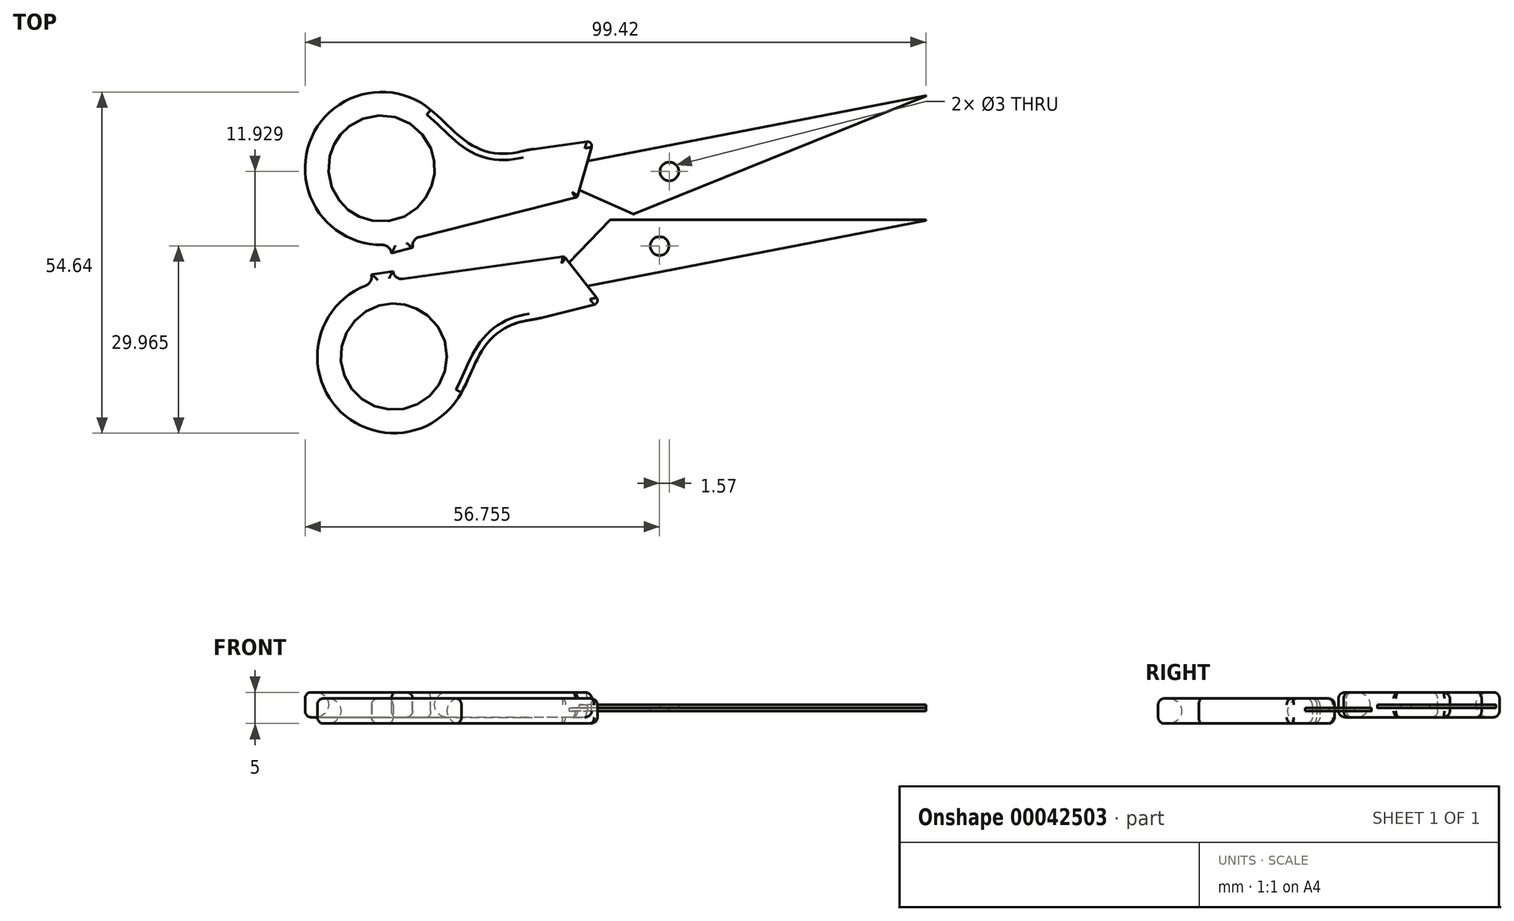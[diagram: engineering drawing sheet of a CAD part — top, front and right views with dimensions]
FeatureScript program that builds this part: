
annotation { "Feature Type Name" : "Feature", "Feature Type Description" : "" }
export const myFeature = defineFeature(function(context is Context, id is Id, definition is map)
    precondition{}
    {
        {
            var Q0;
            Q0=qCreatedBy(makeId("Top.planeOp"),FACE);
            var sketch = newSketch(context, id + "F0", { "sketchPlane" : qUnion([Q0])});
            skLineSegment(sketch, "E0", {"start": v(0.08, 0) * mm, "end": v(50.48, 0) * mm});
            skLineSegment(sketch, "E1", {"start": v(50.5, -0.1) * mm, "end": v(-3.64, -10.62) * mm});
            skLineSegment(sketch, "E2", {"start": v(-0.06, -0.06) * mm, "end": v(-6.6, -6.83) * mm});
            skLineSegment(sketch, "E3", {"start": v(-6.6, -6.83) * mm, "end": v(-3.64, -10.62) * mm});
            skPoint(sketch, "E4.visualSharp", {"position": v(51, 0) * mm});
            skArc(sketch, "E4.filletArc", {"start": v(50.5, -0.1) * mm, "mid": v(50.53, -0.05) * mm, "end": v(50.48, 0) * mm});
            skPoint(sketch, "E5.visualSharp", {"position": v(0, 0) * mm});
            skArc(sketch, "E5.filletArc", {"start": v(0.08, 0) * mm, "mid": v(0, -0.02) * mm, "end": v(-0.06, -0.06) * mm});
            skLineSegment(sketch, "E6", {"start": v(-6.6, -6.83) * mm, "end": v(-7.16, -6.12) * mm});
            skLineSegment(sketch, "E7", {"start": v(-3.64, -10.62) * mm, "end": v(-2.2, -12.47) * mm});
            skLineSegment(sketch, "E8", {"start": v(-3.64, -10.62) * mm, "end": v(-34.65, -21.9) * mm, "construction": true});
            skCircle(sketch, "E9", {"center": v(-34.65, -21.9) * mm, "radius": 8.5 * mm});
            skCircle(sketch, "E10", {"center": v(-34.65, -21.9) * mm, "radius": 12.25 * mm, "construction": true});
            skLineSegment(sketch, "E11", {"start": v(-7.62, -5.93) * mm, "end": v(-33.2, -9.47) * mm});
            skLineSegment(sketch, "E12", {"start": v(-2.58, -13.58) * mm, "end": v(-10.9, -15.66) * mm});
            skFitSpline(sketch, "E13", {"points": [v(-23.83, -27.66) * mm, v(-12.03, -15.94) * mm], "startDerivative": vector(7.63, 13.41) * mm, "endDerivative": vector(25.84, 2.61) * mm});
            skLineSegment(sketch, "E14", {"start": v(-34.65, -21.9) * mm, "end": v(-18.73, -30.37) * mm, "construction": true});
            skLineSegment(sketch, "E15", {"start": v(-34.77, -8.27) * mm, "end": v(-34.77, -8.27) * mm});
            skLineSegment(sketch, "E16", {"start": v(-34.77, -8.27) * mm, "end": v(-38.24, -8.75) * mm});
            skLineSegment(sketch, "E17", {"start": v(-38.24, -8.75) * mm, "end": v(-38.21, -8.91) * mm});
            skArc(sketch, "E18", {"start": v(-39.15, -10.51) * mm, "mid": v(-43.79, -30.07) * mm, "end": v(-23.83, -27.66) * mm});
            skPoint(sketch, "E19.visualSharp", {"position": v(-1.53, -13.32) * mm});
            skArc(sketch, "E19.filletArc", {"start": v(-2.58, -13.58) * mm, "mid": v(-2.08, -13.13) * mm, "end": v(-2.2, -12.47) * mm});
            skPoint(sketch, "E20.visualSharp", {"position": v(-7.34, -5.89) * mm});
            skArc(sketch, "E20.filletArc", {"start": v(-7.16, -6.12) * mm, "mid": v(-7.37, -5.96) * mm, "end": v(-7.62, -5.93) * mm});
            skPoint(sketch, "E21.visualSharp", {"position": v(-34.58, -9.66) * mm});
            skArc(sketch, "E21.filletArc", {"start": v(-34.77, -8.27) * mm, "mid": v(-34.23, -9.2) * mm, "end": v(-33.2, -9.47) * mm});
            skPoint(sketch, "E22.visualSharp", {"position": v(-38.05, -10.14) * mm});
            skArc(sketch, "E22.filletArc", {"start": v(-39.15, -10.51) * mm, "mid": v(-38.4, -9.88) * mm, "end": v(-38.21, -8.91) * mm});
            skPoint(sketch, "E23", {"position": v(13.7, -7.25) * mm});
            skArc(sketch, "E24.filletArc", {"start": v(-12.8, -16.04) * mm, "mid": v(-11.85, -15.87) * mm, "end": v(-10.9, -15.66) * mm});
            skSolve(sketch);
        }
        {
            var Q0;
            Q0=makeQuery(id+"F0.imprint","IMPRINT",FACE,{"disambiguationData":[TD([[makeQuery(id+"F0.imprint","IMPRINT",EDGE,{"derivedFrom":sQuery(id+"F0.wireOp",EDGE,"E0")}),-1.0]])]});
            extrude(context, id + "F1", {"entities" : qUnion([Q0]), "depth" : 0.5 * mm});
        }
        {
            var Q0;
            Q0=makeQuery(id+"F0.imprint","IMPRINT",FACE,{"disambiguationData":[TD([[makeQuery(id+"F0.imprint","IMPRINT",EDGE,{"derivedFrom":sQuery(id+"F0.wireOp",EDGE,"E3")}),-1.0]])]});
            extrude(context, id + "F2", {"entities" : qUnion([Q0]), "operationType" : NewBodyOperationType.ADD, "endBound" : BoundingType.SYMMETRIC, "depth" : 4 * mm});
        }
        {
            var Q0;
            Q0=makeQuery(id+"F2.opExtrude","CAP_EDGE",EDGE,{"disambiguationData":[OSD([sQuery(id+"F0.wireOp",EDGE,"E3"),sQuery(id+"F0.wireOp",EDGE,"E6"),sQuery(id+"F0.wireOp",EDGE,"E7")])],"isStart":false});
            var Q1;
            Q1=makeQuery(id+"F2.opExtrude","CAP_EDGE",EDGE,{"disambiguationData":[OSD([sQuery(id+"F0.wireOp",EDGE,"E11")])],"isStart":false});
            var Q2;
            Q2=makeQuery(id+"F2.opExtrude","CAP_EDGE",EDGE,{"disambiguationData":[OSD([sQuery(id+"F0.wireOp",EDGE,"E18")])],"isStart":false});
            var Q3;
            Q3=makeQuery(id+"F2.opExtrude","CAP_EDGE",EDGE,{"disambiguationData":[OSD([sQuery(id+"F0.wireOp",EDGE,"E19.filletArc")])],"isStart":false});
            var Q4;
            Q4=makeQuery(id+"F2.opExtrude","CAP_EDGE",EDGE,{"disambiguationData":[OSD([sQuery(id+"F0.wireOp",EDGE,"E12")])],"isStart":false});
            var Q5;
            Q5=makeQuery(id+"F2.opExtrude","CAP_EDGE",EDGE,{"disambiguationData":[OSD([sQuery(id+"F0.wireOp",EDGE,"E16")])],"isStart":false});
            var Q6;
            Q6=makeQuery(id+"F2.opExtrude","CAP_EDGE",EDGE,{"disambiguationData":[OSD([sQuery(id+"F0.wireOp",EDGE,"E13")])],"isStart":false});
            var Q7;
            Q7=makeQuery(id+"F2.opExtrude","CAP_EDGE",EDGE,{"disambiguationData":[OSD([sQuery(id+"F0.wireOp",EDGE,"E21.filletArc")])],"isStart":false});
            var Q8;
            Q8=makeQuery(id+"F2.opExtrude","CAP_EDGE",EDGE,{"disambiguationData":[OSD([sQuery(id+"F0.wireOp",EDGE,"E22.filletArc")])],"isStart":false});
            var Q9;
            Q9=makeQuery(id+"F2.opExtrude","CAP_EDGE",EDGE,{"disambiguationData":[OSD([sQuery(id+"F0.wireOp",EDGE,"E20.filletArc")])],"isStart":false});
            var Q10;
            Q10=makeQuery(id+"F2.opExtrude","CAP_EDGE",EDGE,{"disambiguationData":[OSD([sQuery(id+"F0.wireOp",EDGE,"E17")])],"isStart":false});
            var Q11;
            Q11=makeQuery(id+"F2.opExtrude","CAP_EDGE",EDGE,{"disambiguationData":[OSD([sQuery(id+"F0.wireOp",EDGE,"E3"),sQuery(id+"F0.wireOp",EDGE,"E6"),sQuery(id+"F0.wireOp",EDGE,"E7")])],"isStart":true});
            var Q12;
            Q12=makeQuery(id+"F2.opExtrude","CAP_EDGE",EDGE,{"disambiguationData":[OSD([sQuery(id+"F0.wireOp",EDGE,"E18")])],"isStart":true});
            var Q13;
            Q13=makeQuery(id+"F2.opExtrude","CAP_EDGE",EDGE,{"disambiguationData":[OSD([sQuery(id+"F0.wireOp",EDGE,"E11")])],"isStart":true});
            var Q14;
            Q14=makeQuery(id+"F2.opExtrude","CAP_EDGE",EDGE,{"disambiguationData":[OSD([sQuery(id+"F0.wireOp",EDGE,"E22.filletArc")])],"isStart":true});
            var Q15;
            Q15=makeQuery(id+"F2.opExtrude","CAP_EDGE",EDGE,{"disambiguationData":[OSD([sQuery(id+"F0.wireOp",EDGE,"E20.filletArc")])],"isStart":true});
            var Q16;
            Q16=makeQuery(id+"F2.opExtrude","CAP_EDGE",EDGE,{"disambiguationData":[OSD([sQuery(id+"F0.wireOp",EDGE,"E12")])],"isStart":true});
            var Q17;
            Q17=makeQuery(id+"F2.opExtrude","CAP_EDGE",EDGE,{"disambiguationData":[OSD([sQuery(id+"F0.wireOp",EDGE,"E13")])],"isStart":true});
            var Q18;
            Q18=makeQuery(id+"F2.opExtrude","CAP_EDGE",EDGE,{"disambiguationData":[OSD([sQuery(id+"F0.wireOp",EDGE,"E16")])],"isStart":true});
            var Q19;
            Q19=makeQuery(id+"F2.opExtrude","CAP_EDGE",EDGE,{"disambiguationData":[OSD([sQuery(id+"F0.wireOp",EDGE,"E21.filletArc")])],"isStart":true});
            var Q20;
            Q20=makeQuery(id+"F2.opExtrude","CAP_EDGE",EDGE,{"disambiguationData":[OSD([sQuery(id+"F0.wireOp",EDGE,"E19.filletArc")])],"isStart":true});
            fillet(context, id + "F3", {"entities" : qUnion([Q0, Q1, Q2, Q3, Q4, Q5, Q6, Q7, Q8, Q9, Q10, Q11, Q12, Q13, Q14, Q15, Q16, Q17, Q18, Q19, Q20]), "radius" : 1 * mm, "tangentPropagation" : true, "allowEdgeOverflow" : false});
        }
        {
            var Q0;
            Q0=makeQuery(id+"F2.opExtrude","CAP_EDGE",EDGE,{"disambiguationData":[OSD([sQuery(id+"F0.wireOp",EDGE,"E9")])],"isStart":false});
            fillet(context, id + "F4", {"entities" : qUnion([Q0]), "radius" : 2 * mm, "tangentPropagation" : true, "allowEdgeOverflow" : false});
        }
        {
            var Q0;
            Q0=makeQuery(id+"F2.opExtrude","CAP_EDGE",EDGE,{"disambiguationData":[OSD([sQuery(id+"F0.wireOp",EDGE,"E9")])],"isStart":true});
            fillet(context, id + "F5", {"entities" : qUnion([Q0]), "radius" : 2 * mm, "tangentPropagation" : true, "allowEdgeOverflow" : false});
        }
        {
            var Q0;
            Q0=makeQuery(id+"F1.opExtrude","SWEPT_BODY",BODY,{"disambiguationData":[OSD([sQuery(id+"F0.wireOp",EDGE,"E0"),sQuery(id+"F0.wireOp",EDGE,"E1"),sQuery(id+"F0.wireOp",EDGE,"E2"),sQuery(id+"F0.wireOp",EDGE,"E3"),sQuery(id+"F0.wireOp",EDGE,"E4.filletArc"),sQuery(id+"F0.wireOp",EDGE,"E5.filletArc")])]});
            transform(context, id + "F6", {"entities" : qUnion([Q0]), "transformType" : TransformType.TRANSLATION_3D, "dx" : 0 * mm, "dy" : 29.41 * mm, "dz" : 0 * mm, "makeCopy" : true});
        }
        {
            var Q0;
            Q0=makeQuery(id+"F6.opPattern","COPY",BODY,{"derivedFrom":makeQuery(id+"F1.opExtrude","SWEPT_BODY",BODY,{"disambiguationData":[OSD([sQuery(id+"F0.wireOp",EDGE,"E0"),sQuery(id+"F0.wireOp",EDGE,"E1"),sQuery(id+"F0.wireOp",EDGE,"E2"),sQuery(id+"F0.wireOp",EDGE,"E3"),sQuery(id+"F0.wireOp",EDGE,"E4.filletArc"),sQuery(id+"F0.wireOp",EDGE,"E5.filletArc")])]}),"instanceName":"1"});
            deleteBodies(context, id + "F7", {"entities" : qUnion([Q0])});
        }
        {
            var Q0;
            Q0=makeQuery(id+"F1.opExtrude","CAP_FACE",FACE,{"disambiguationData":[OSD([sQuery(id+"F0.wireOp",EDGE,"E0"),sQuery(id+"F0.wireOp",EDGE,"E1"),sQuery(id+"F0.wireOp",EDGE,"E2"),sQuery(id+"F0.wireOp",EDGE,"E3"),sQuery(id+"F0.wireOp",EDGE,"E4.filletArc"),sQuery(id+"F0.wireOp",EDGE,"E5.filletArc")])],"isStart":false});
            var sketch = newSketch(context, id + "F8", { "sketchPlane" : qUnion([Q0])});
            skLineSegment(sketch, "E25", {"start": v(0.08, 0) * mm, "end": v(7.88, 0) * mm, "construction": true});
            skLineSegment(sketch, "E26", {"start": v(7.88, 0) * mm, "end": v(7.88, -8.38) * mm, "construction": true});
            skCircle(sketch, "E27", {"center": v(7.88, -4.2) * mm, "radius": 1.5 * mm});
            skSolve(sketch);
        }
        {
            var Q0;
            Q0=makeQuery(id+"F8.imprint","IMPRINT",FACE,{"disambiguationData":[TD([[makeQuery(id+"F8.imprint","IMPRINT",EDGE,{"derivedFrom":sQuery(id+"F8.wireOp",EDGE,"E27")}),1.0]])]});
            extrude(context, id + "F9", {"entities" : qUnion([Q0]), "operationType" : NewBodyOperationType.REMOVE, "oppositeDirection" : true, "depth" : 2 * mm});
        }
        {
            var Q0;
            Q0=makeQuery(id+"F1.opExtrude","SWEPT_BODY",BODY,{"disambiguationData":[OSD([sQuery(id+"F0.wireOp",EDGE,"E0"),sQuery(id+"F0.wireOp",EDGE,"E1"),sQuery(id+"F0.wireOp",EDGE,"E2"),sQuery(id+"F0.wireOp",EDGE,"E3"),sQuery(id+"F0.wireOp",EDGE,"E4.filletArc"),sQuery(id+"F0.wireOp",EDGE,"E5.filletArc")])]});
            transform(context, id + "F10", {"entities" : qUnion([Q0]), "transformType" : TransformType.TRANSLATION_3D, "dx" : 0 * mm, "dy" : 36 * mm, "dz" : 0 * mm, "makeCopy" : true});
        }
        {
            var Q0;
            Q0=makeQuery(id+"F10.opPattern","COPY",BODY,{"derivedFrom":makeQuery(id+"F1.opExtrude","SWEPT_BODY",BODY,{"disambiguationData":[OSD([sQuery(id+"F0.wireOp",EDGE,"E0"),sQuery(id+"F0.wireOp",EDGE,"E1"),sQuery(id+"F0.wireOp",EDGE,"E2"),sQuery(id+"F0.wireOp",EDGE,"E3"),sQuery(id+"F0.wireOp",EDGE,"E4.filletArc"),sQuery(id+"F0.wireOp",EDGE,"E5.filletArc")])]}),"instanceName":"1"});
            var Q1;
            Q1=makeQuery(id+"F10.opPattern","COPY",EDGE,{"derivedFrom":makeQuery(id+"F1.opExtrude","CAP_EDGE",EDGE,{"disambiguationData":[OSD([sQuery(id+"F0.wireOp",EDGE,"E1")])],"isStart":false}),"instanceName":"1"});
            transform(context, id + "F11", {"entities" : qUnion([Q0]), "transformType" : TransformType.ROTATION, "transformAxis" : qUnion([Q1]), "angle" : 180 * degree, "makeCopy" : false});
        }
        {
            var Q0;
            Q0=makeQuery(id+"F1.opExtrude","SWEPT_BODY",BODY,{"disambiguationData":[OSD([sQuery(id+"F0.wireOp",EDGE,"E0"),sQuery(id+"F0.wireOp",EDGE,"E1"),sQuery(id+"F0.wireOp",EDGE,"E2"),sQuery(id+"F0.wireOp",EDGE,"E3"),sQuery(id+"F0.wireOp",EDGE,"E4.filletArc"),sQuery(id+"F0.wireOp",EDGE,"E5.filletArc")])]});
            transform(context, id + "F12", {"entities" : qUnion([Q0]), "transformType" : TransformType.TRANSLATION_3D, "dx" : 0 * mm, "dy" : 16 * mm, "dz" : 0 * mm, "makeCopy" : false});
        }
    });
